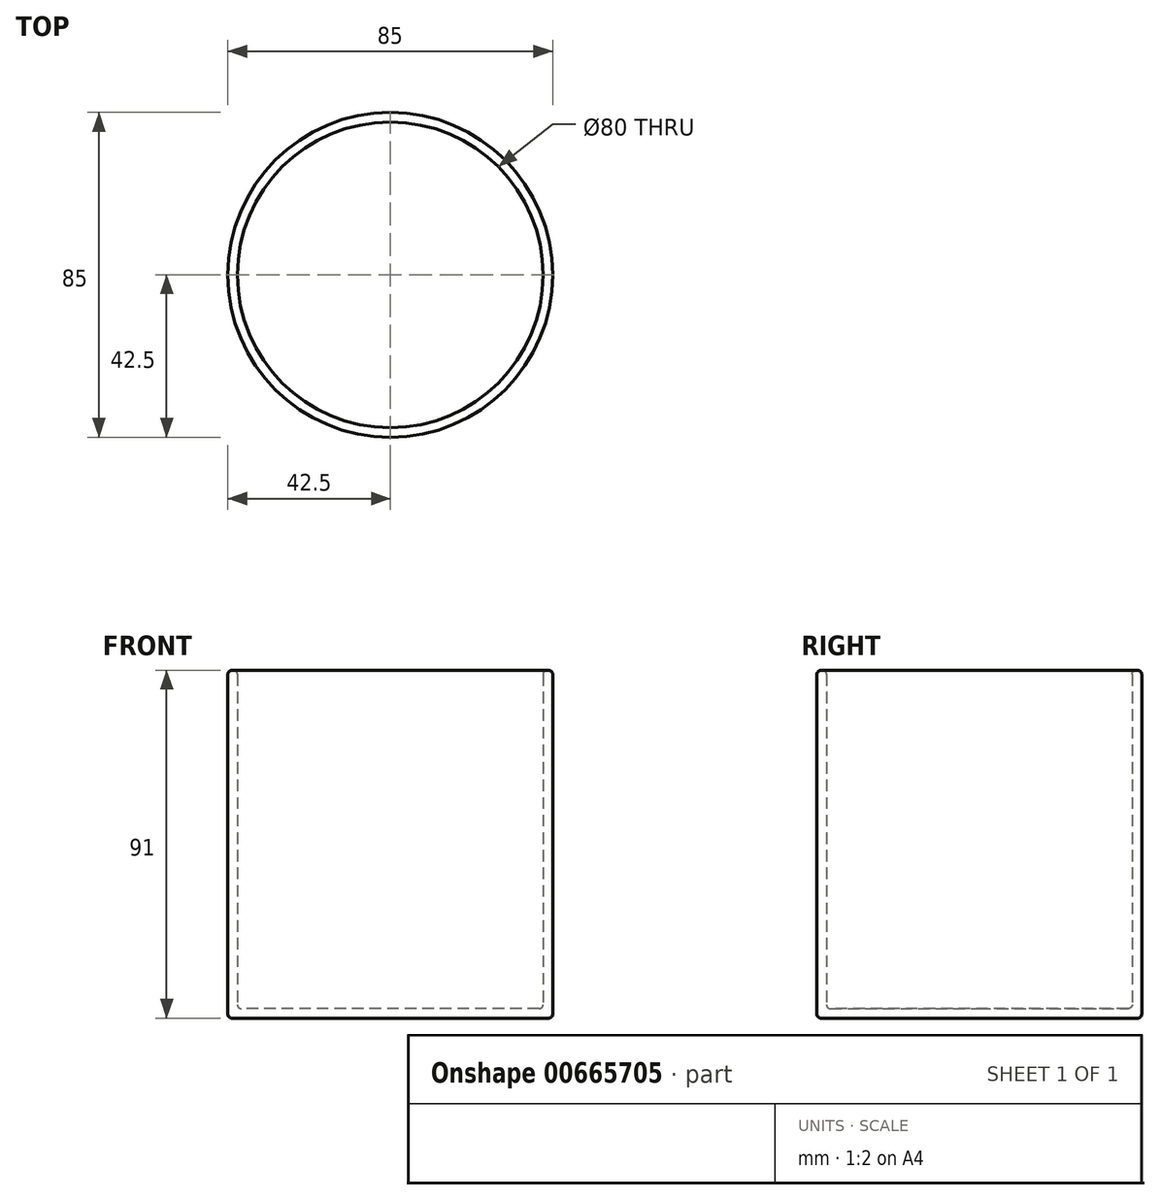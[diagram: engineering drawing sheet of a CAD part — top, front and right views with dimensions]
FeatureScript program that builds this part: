
annotation { "Feature Type Name" : "Feature", "Feature Type Description" : "" }
export const myFeature = defineFeature(function(context is Context, id is Id, definition is map)
    precondition{}
    {
        {
            var Q0;
            Q0=qCreatedBy(makeId("Top.planeOp"),FACE);
            var sketch = newSketch(context, id + "F0", { "sketchPlane" : qUnion([Q0])});
            skCircle(sketch, "E0", {"center": v(0, 0) * mm, "radius": 42.5 * mm});
            skSolve(sketch);
        }
        {
            var Q0;
            Q0=makeQuery(id+"F0.imprint","IMPRINT",FACE,{"disambiguationData":[TD([[makeQuery(id+"F0.imprint","IMPRINT",EDGE,{"derivedFrom":sQuery(id+"F0.wireOp",EDGE,"E0")}),1.0]])]});
            extrude(context, id + "F1", {"entities" : qUnion([Q0]), "depth" : 91 * mm, "offsetDistance" : 25 * mm});
        }
        {
            var Q0;
            Q0=qCreatedBy(makeId("Right.planeOp"),FACE);
            cPlane(context, id + "F2", {"entities" : qUnion([Q0]), "cplaneType" : CPlaneType.OFFSET, "offset" : 40 * mm, "width" : 150 * mm, "height" : 150 * mm});
        }
        {
            var Q0;
            Q0=qCreatedBy(id+"F2.planeOp",FACE);
            var sketch = newSketch(context, id + "F3", { "sketchPlane" : qUnion([Q0])});
            skCircle(sketch, "E1", {"center": v(2.03, 20.49) * mm, "radius": 7.13 * mm});
            skSolve(sketch);
        }
        {
            var Q0;
            Q0=qCreatedBy(makeId("Front.planeOp"),FACE);
            var sketch = newSketch(context, id + "F4", { "sketchPlane" : qUnion([Q0])});
            skFitSpline(sketch, "E2", {"points": [v(38.6, 65.17) * mm, v(54.27, 69.74) * mm, v(64.19, 59.99) * mm, v(68.15, 39.48) * mm, v(63.66, 19.08) * mm, v(51.04, 11.78) * mm, v(39.35, 18.17) * mm], "startDerivative": vector(100.42, 49.92) * mm, "endDerivative": vector(-74.4, 62.1) * mm});
            skSolve(sketch);
        }
        {
            var Q0;
            Q0=makeQuery(id+"F1.opExtrude","CAP_FACE",FACE,{"disambiguationData":[OSD([sQuery(id+"F0.wireOp",EDGE,"E0")])],"isStart":false});
            shell(context, id + "F5", {"entities" : qUnion([Q0]), "thickness" : 2.5 * mm});
        }
        {
            var Q0;
            {var subQ0=sQuery(id+"F0.wireOp",EDGE,"E0");Q0=makeQuery(id+"F5.opShell","OFFSET_FACE",FACE,{"disambiguationData":[OSD([subQ0]),TDD([makeQuery(id+"F1.opExtrude","CAP_FACE",FACE,{"disambiguationData":[OSD([subQ0])],"isStart":true})])]});}
            var Q1;
            Q1=makeQuery(id+"F1.opExtrude","SWEPT_FACE",FACE,{"disambiguationData":[OSD([sQuery(id+"F0.wireOp",EDGE,"E0")])]});
            var Q2;
            {var subQ0=sQuery(id+"F0.wireOp",EDGE,"E0");Q2=makeQuery(id+"F5.opShell","OFFSET_FACE",FACE,{"disambiguationData":[OSD([subQ0]),TDD([makeQuery(id+"F1.opExtrude","SWEPT_FACE",FACE,{"disambiguationData":[OSD([subQ0])]})])]});}
            fillet(context, id + "F6", {"entities" : qUnion([Q0, Q1, Q2]), "radius" : 1 * mm, "tangentPropagation" : true, "allowEdgeOverflow" : false});
        }
    });
